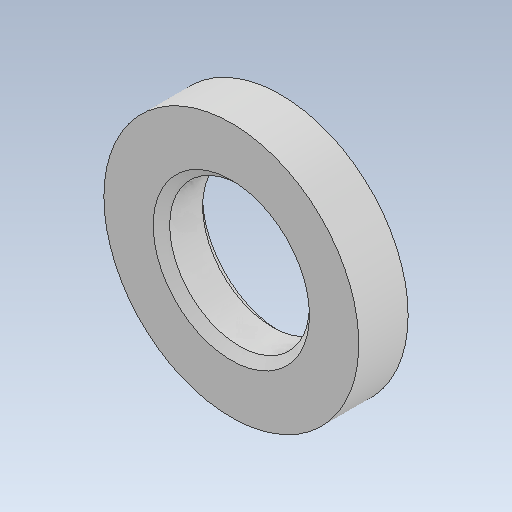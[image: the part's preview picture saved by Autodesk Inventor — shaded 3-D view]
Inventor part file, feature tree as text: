
AUTODESK INVENTOR PART (.ipt)
format: ipt  version: 2020 (Build 240168000, 168)  size: 115,712 bytes
history: native  units: mm
features: other x3, sketch x1, plane x1, extrude x1, chamfer x1, reference x1
ambient origin geometry x8: Origin, YZ Plane, XZ Plane, XY Plane, X Axis, Y Axis, Z Axis, Center Point
bodies: Solid1 (feature_tree)
feature tree (8):
  sketch  "Sketch1"  dims[d0=8.5mm d1=15.5mm d2=10.0mm d3=0.0mm d4=0.5mm d5=2.0mm d6=45.0deg]
  plane  "Work Plane1"
  extrude  "Extrusion1"  Depth=10.0mm
  chamfer  "Chamfer1"  Distance=10.0mm
  reference  "Reference1"
  parser-record x1  (decoder bookkeeping rows leaked as tree rows — omitted from the tree; the rows remain in map.json)
  other  "reducer_1.iam"
  other  "bearing_8_16_5:6"
note: 1 file-system path scrubbed to <path> (originals preserved in map.json)
